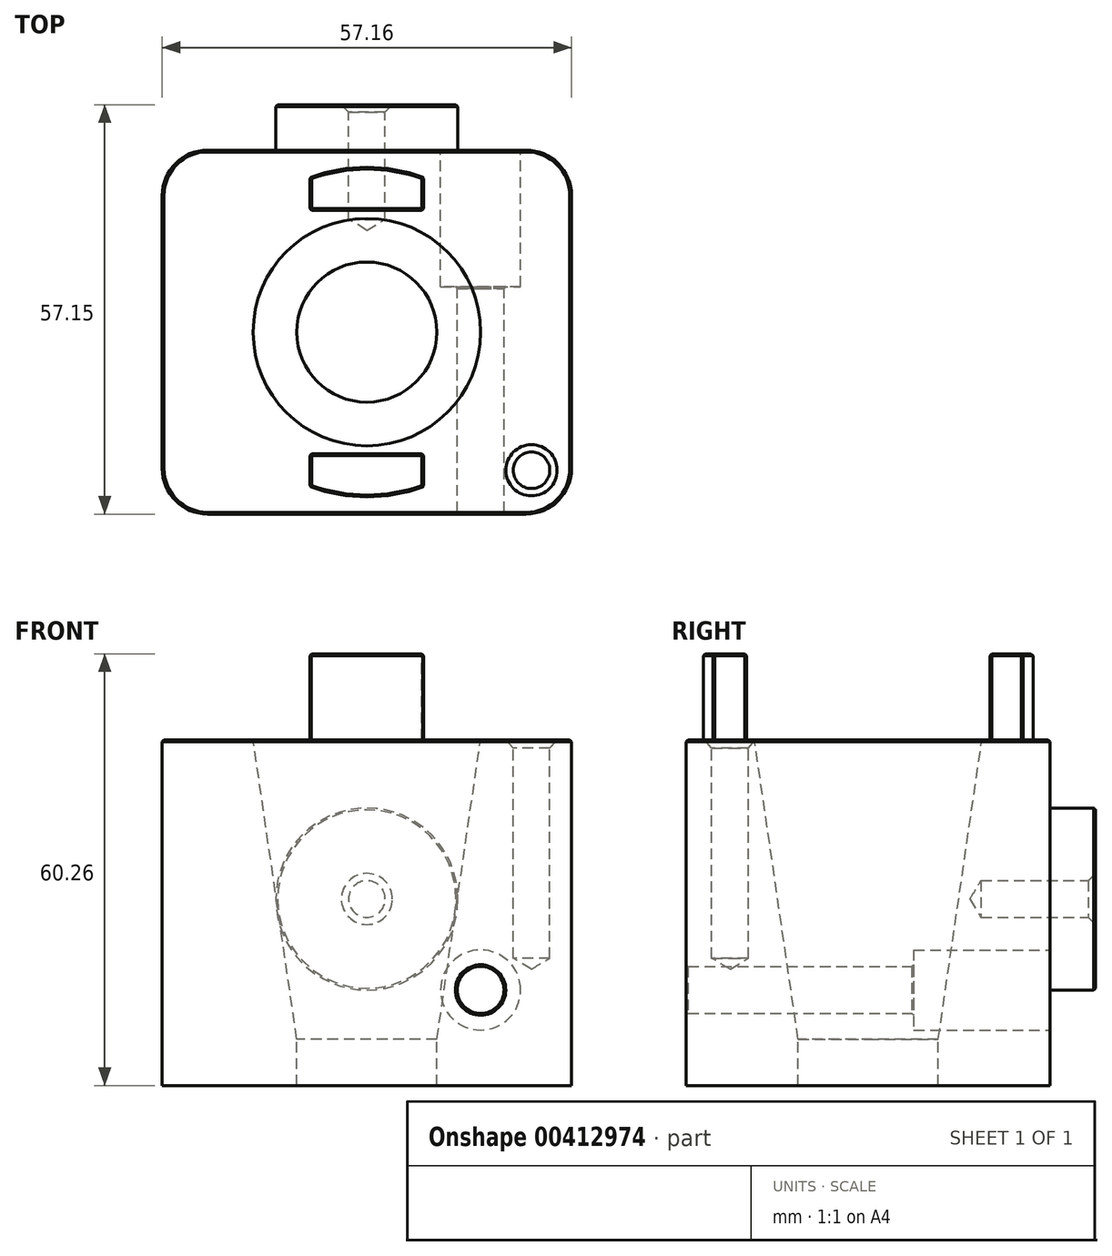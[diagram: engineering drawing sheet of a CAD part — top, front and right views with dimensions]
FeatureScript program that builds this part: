
annotation { "Feature Type Name" : "Feature", "Feature Type Description" : "" }
export const myFeature = defineFeature(function(context is Context, id is Id, definition is map)
    precondition{}
    {
        {
            var Q0;
            Q0=qCreatedBy(makeId("Top.planeOp"),FACE);
            var sketch = newSketch(context, id + "F0", { "sketchPlane" : qUnion([Q0])});
            skLineSegment(sketch, "E0.bottom", {"start": v(28.58, -25.4) * mm, "end": v(-28.58, -25.4) * mm});
            skLineSegment(sketch, "E0.top", {"start": v(28.58, 25.4) * mm, "end": v(-28.58, 25.4) * mm});
            skLineSegment(sketch, "E0.left", {"start": v(28.57, -25.4) * mm, "end": v(28.58, 25.4) * mm});
            skLineSegment(sketch, "E0.right", {"start": v(-28.58, -25.4) * mm, "end": v(-28.58, 25.4) * mm});
            skPoint(sketch, "E0.middle", {"position": v(0, 0) * mm});
            skSolve(sketch);
        }
        {
            var Q0;
            Q0 = qSketchRegion(id + "F0", true);
            extrude(context, id + "F1", {"entities" : qUnion([Q0]), "oppositeDirection" : true, "depth" : 48.26 * mm});
        }
        {
            var Q0;
            Q0=qCreatedBy(makeId("Front.planeOp"),FACE);
            var sketch = newSketch(context, id + "F2", { "sketchPlane" : qUnion([Q0])});
            skLineSegment(sketch, "E1", {"start": v(0, 0) * mm, "end": v(15.88, 0) * mm});
            skLineSegment(sketch, "E2", {"start": v(15.88, 0) * mm, "end": v(9.78, -41.8) * mm});
            skLineSegment(sketch, "E3", {"start": v(9.78, -48.4) * mm, "end": v(0, -48.4) * mm});
            skLineSegment(sketch, "E4", {"start": v(0, -48.4) * mm, "end": v(0, 0) * mm});
            skLineSegment(sketch, "E5", {"start": v(9.78, -48.4) * mm, "end": v(9.78, -41.8) * mm});
            skSolve(sketch);
        }
        {
            var Q0;
            Q0 = qSketchRegion(id + "F2", true);
            var Q1;
            Q1=sQuery(id+"F2.wireOp",EDGE,"E4");
            revolve(context, id + "F3", {"operationType" : NewBodyOperationType.REMOVE, "entities" : qUnion([Q0]), "axis" : qUnion([Q1]), "revolveType" : RevolveType.FULL, "oppositeDirection" : true});
        }
        {
            var Q0;
            Q0=makeQuery(id+"F1.opExtrude","CAP_FACE",FACE,{"disambiguationData":[OSD([sQuery(id+"F0.wireOp",EDGE,"E0.bottom"),sQuery(id+"F0.wireOp",EDGE,"E0.top"),sQuery(id+"F0.wireOp",EDGE,"E0.left"),sQuery(id+"F0.wireOp",EDGE,"E0.right")])],"isStart":true});
            var sketch = newSketch(context, id + "F4", { "sketchPlane" : qUnion([Q0])});
            skLineSegment(sketch, "E6", {"start": v(-7.94, 21.59) * mm, "end": v(-7.94, 17) * mm});
            skLineSegment(sketch, "E7", {"start": v(7.94, 21.59) * mm, "end": v(7.94, 17) * mm});
            skLineSegment(sketch, "E8", {"start": v(-7.94, 17) * mm, "end": v(7.94, 17) * mm});
            skLineSegment(sketch, "E9", {"start": v(-7.94, -17) * mm, "end": v(7.94, -17) * mm});
            skArc(sketch, "E10", {"start": v(7.94, 21.59) * mm, "mid": v(0, 23) * mm, "end": v(-7.94, 21.59) * mm});
            skArc(sketch, "E11.trimOffspring", {"start": v(-7.94, -21.59) * mm, "mid": v(0, -23) * mm, "end": v(7.94, -21.59) * mm});
            skLineSegment(sketch, "E12.trimOffspring", {"start": v(-7.94, -17) * mm, "end": v(-7.94, -21.59) * mm});
            skLineSegment(sketch, "E13.trimOffspring", {"start": v(7.94, -17) * mm, "end": v(7.94, -21.59) * mm});
            skSolve(sketch);
        }
        {
            var Q0;
            Q0 = qSketchRegion(id + "F4", true);
            extrude(context, id + "F5", {"entities" : qUnion([Q0]), "operationType" : NewBodyOperationType.ADD, "depth" : 12 * mm});
        }
        {
            var Q0;
            Q0=makeQuery(id+"F1.opExtrude","SWEPT_FACE",FACE,{"disambiguationData":[OSD([sQuery(id+"F0.wireOp",EDGE,"E0.top")])]});
            var sketch = newSketch(context, id + "F6", { "sketchPlane" : qUnion([Q0])});
            skCircle(sketch, "E14", {"center": v(-15.87, -34.93) * mm, "radius": 3.26 * mm});
            skSolve(sketch);
        }
        {
            var Q0;
            Q0 = qSketchRegion(id + "F6", true);
            extrude(context, id + "F7", {"entities" : qUnion([Q0]), "operationType" : NewBodyOperationType.REMOVE, "endBound" : BoundingType.THROUGH_ALL, "oppositeDirection" : true, "depth" : 25.4 * mm});
        }
        {
            var Q0;
            Q0=makeQuery(id+"F1.opExtrude","SWEPT_EDGE",EDGE,{"disambiguationData":[OSD([sQuery(id+"F0.wireOp",EDGE,"E0.bottom"),sQuery(id+"F0.wireOp",EDGE,"E0.right")])]});
            var Q1;
            Q1=makeQuery(id+"F1.opExtrude","SWEPT_EDGE",EDGE,{"disambiguationData":[OSD([sQuery(id+"F0.wireOp",EDGE,"E0.bottom"),sQuery(id+"F0.wireOp",EDGE,"E0.left")])]});
            var Q2;
            Q2=makeQuery(id+"F1.opExtrude","SWEPT_EDGE",EDGE,{"disambiguationData":[OSD([sQuery(id+"F0.wireOp",EDGE,"E0.top"),sQuery(id+"F0.wireOp",EDGE,"E0.left")])]});
            var Q3;
            Q3=makeQuery(id+"F1.opExtrude","SWEPT_EDGE",EDGE,{"disambiguationData":[OSD([sQuery(id+"F0.wireOp",EDGE,"E0.top"),sQuery(id+"F0.wireOp",EDGE,"E0.right")])]});
            fillet(context, id + "F8", {"entities" : qUnion([Q0, Q1, Q2, Q3]), "radius" : 6.35 * mm, "tangentPropagation" : true, "allowEdgeOverflow" : false});
        }
        {
            var Q0;
            Q0=makeQuery(id+"F1.opExtrude","CAP_FACE",FACE,{"disambiguationData":[OSD([sQuery(id+"F0.wireOp",EDGE,"E0.bottom"),sQuery(id+"F0.wireOp",EDGE,"E0.top"),sQuery(id+"F0.wireOp",EDGE,"E0.left"),sQuery(id+"F0.wireOp",EDGE,"E0.right")])],"isStart":true});
            var sketch = newSketch(context, id + "F9", { "sketchPlane" : qUnion([Q0])});
            skPoint(sketch, "E15", {"position": v(22.98, -19.28) * mm});
            skLineSegment(sketch, "E16", {"start": v(22.98, -19.28) * mm, "end": v(0, 0) * mm, "construction": true});
            skSolve(sketch);
        }
        {
            var Q0;
            Q0=sQuery(id+"F9.wireOp",VERTEX,"E15");
            var Q1;
            Q1=makeQuery(id+"F1.opExtrude","SWEPT_BODY",BODY,{"disambiguationData":[OSD([sQuery(id+"F0.wireOp",EDGE,"E0.bottom"),sQuery(id+"F0.wireOp",EDGE,"E0.top"),sQuery(id+"F0.wireOp",EDGE,"E0.left"),sQuery(id+"F0.wireOp",EDGE,"E0.right")])]});
            hole(context, id + "F10", {"style" : HoleStyle.C_SINK, "endStyle" : HoleEndStyle.BLIND, "holeDiameter" : 5.1 * mm, "cSinkDiameter" : 7.14 * mm, "cSinkAngle" : 82 * degree, "holeDepth" : 30.48 * mm, "isTappedThrough" : true, "tappedDepth" : 12.7 * mm, "tapClearance" : 3, "startFromSketch" : true, "locations" : qUnion([Q0]), "scope" : qUnion([Q1])});
        }
        {
            var Q0;
            Q0=makeQuery(id+"F1.opExtrude","SWEPT_FACE",FACE,{"disambiguationData":[OSD([sQuery(id+"F0.wireOp",EDGE,"E0.top")])]});
            var sketch = newSketch(context, id + "F11", { "sketchPlane" : qUnion([Q0])});
            skCircle(sketch, "E17", {"center": v(0, -22.23) * mm, "radius": 12.7 * mm});
            skSolve(sketch);
        }
        {
            var Q0;
            Q0 = qSketchRegion(id + "F11", true);
            extrude(context, id + "F12", {"entities" : qUnion([Q0]), "operationType" : NewBodyOperationType.ADD, "depth" : 6.35 * mm});
        }
        {
            var Q0;
            Q0=makeQuery(id+"F1.opExtrude","SWEPT_FACE",FACE,{"disambiguationData":[OSD([sQuery(id+"F0.wireOp",EDGE,"E0.top")])]});
            var sketch = newSketch(context, id + "F13", { "sketchPlane" : qUnion([Q0])});
            skCircle(sketch, "E18", {"center": v(-15.87, -34.93) * mm, "radius": 5.59 * mm});
            skSolve(sketch);
        }
        {
            var Q0;
            Q0 = qSketchRegion(id + "F13", true);
            extrude(context, id + "F14", {"entities" : qUnion([Q0]), "operationType" : NewBodyOperationType.REMOVE, "oppositeDirection" : true, "depth" : 19.05 * mm});
        }
        {
            var Q0;
            Q0=makeQuery(id+"F12.opExtrude","CAP_FACE",FACE,{"disambiguationData":[OSD([sQuery(id+"F11.wireOp",EDGE,"E17")])],"isStart":false});
            var sketch = newSketch(context, id + "F15", { "sketchPlane" : qUnion([Q0])});
            skPoint(sketch, "E19", {"position": v(0, -22.23) * mm});
            skSolve(sketch);
        }
        {
            var Q0;
            Q0=sQuery(id+"F15.wireOp",VERTEX,"E19");
            var Q1;
            Q1=makeQuery(id+"F1.opExtrude","SWEPT_BODY",BODY,{"disambiguationData":[OSD([sQuery(id+"F0.wireOp",EDGE,"E0.bottom"),sQuery(id+"F0.wireOp",EDGE,"E0.top"),sQuery(id+"F0.wireOp",EDGE,"E0.left"),sQuery(id+"F0.wireOp",EDGE,"E0.right")])]});
            hole(context, id + "F16", {"style" : HoleStyle.C_SINK, "endStyle" : HoleEndStyle.BLIND, "holeDiameter" : 5.1 * mm, "cSinkDiameter" : 7.14 * mm, "cSinkAngle" : 90 * degree, "holeDepth" : 16 * mm, "isTappedThrough" : true, "tappedDepth" : 12.7 * mm, "tapClearance" : 3, "startFromSketch" : true, "locations" : qUnion([Q0]), "scope" : qUnion([Q1])});
        }
        {
            var Q0;
            Q0=makeQuery(id+"F5.opExtrude","CAP_FACE",FACE,{"disambiguationData":[OSD([sQuery(id+"F4.wireOp",EDGE,"E9"),sQuery(id+"F4.wireOp",EDGE,"E11.trimOffspring"),sQuery(id+"F4.wireOp",EDGE,"E12.trimOffspring"),sQuery(id+"F4.wireOp",EDGE,"E13.trimOffspring")])],"isStart":false});
            var Q1;
            Q1=makeQuery(id+"F5.opExtrude","CAP_FACE",FACE,{"disambiguationData":[OSD([sQuery(id+"F4.wireOp",EDGE,"E6"),sQuery(id+"F4.wireOp",EDGE,"E7"),sQuery(id+"F4.wireOp",EDGE,"E8"),sQuery(id+"F4.wireOp",EDGE,"E10")])],"isStart":false});
            var Q2;
            Q2=makeQuery(id+"F5.opExtrude","SWEPT_EDGE",EDGE,{"disambiguationData":[OSD([sQuery(id+"F4.wireOp",EDGE,"E7"),sQuery(id+"F4.wireOp",EDGE,"E8")])]});
            var Q3;
            Q3=makeQuery(id+"F5.opExtrude","SWEPT_EDGE",EDGE,{"disambiguationData":[OSD([sQuery(id+"F4.wireOp",EDGE,"E9"),sQuery(id+"F4.wireOp",EDGE,"E13.trimOffspring")])]});
            var Q4;
            Q4=makeQuery(id+"F5.opExtrude","SWEPT_EDGE",EDGE,{"disambiguationData":[OSD([sQuery(id+"F4.wireOp",EDGE,"E6"),sQuery(id+"F4.wireOp",EDGE,"E8")])]});
            var Q5;
            Q5=makeQuery(id+"F5.opExtrude","SWEPT_EDGE",EDGE,{"disambiguationData":[OSD([sQuery(id+"F4.wireOp",EDGE,"E9"),sQuery(id+"F4.wireOp",EDGE,"E12.trimOffspring")])]});
            var Q6;
            Q6=makeQuery(id+"F5.opExtrude","SWEPT_EDGE",EDGE,{"disambiguationData":[OSD([sQuery(id+"F4.wireOp",EDGE,"E11.trimOffspring"),sQuery(id+"F4.wireOp",EDGE,"E12.trimOffspring")])]});
            var Q7;
            Q7=makeQuery(id+"F5.opExtrude","SWEPT_EDGE",EDGE,{"disambiguationData":[OSD([sQuery(id+"F4.wireOp",EDGE,"E6"),sQuery(id+"F4.wireOp",EDGE,"E10")])]});
            var Q8;
            Q8=makeQuery(id+"F5.opExtrude","SWEPT_EDGE",EDGE,{"disambiguationData":[OSD([sQuery(id+"F4.wireOp",EDGE,"E7"),sQuery(id+"F4.wireOp",EDGE,"E10")])]});
            var Q9;
            Q9=makeQuery(id+"F5.opExtrude","SWEPT_EDGE",EDGE,{"disambiguationData":[OSD([sQuery(id+"F4.wireOp",EDGE,"E11.trimOffspring"),sQuery(id+"F4.wireOp",EDGE,"E13.trimOffspring")])]});
            var Q10;
            Q10=makeQuery(id+"F1.opExtrude","CAP_EDGE",EDGE,{"disambiguationData":[OSD([sQuery(id+"F0.wireOp",EDGE,"E0.left")])],"isStart":true});
            var Q11;
            {var subQ0=sQuery(id+"F0.wireOp",EDGE,"E0.left");var subQ1=sQuery(id+"F0.wireOp",EDGE,"E0.top");Q11=makeQuery(id+"F8.opFillet","BLEND_EDGE",EDGE,{"blendedFrom":[makeQuery(id+"F1.opExtrude","SWEPT_EDGE",EDGE,{"disambiguationData":[OSD([subQ1,subQ0])]}),makeQuery(id+"F1.opExtrude","CAP_FACE",FACE,{"disambiguationData":[OSD([sQuery(id+"F0.wireOp",EDGE,"E0.bottom"),subQ1,subQ0,sQuery(id+"F0.wireOp",EDGE,"E0.right")])],"isStart":true})],"blendedInto":[makeQuery(id+"F1.opExtrude","CAP_FACE",FACE,{"disambiguationData":[OSD([sQuery(id+"F0.wireOp",EDGE,"E0.bottom"),subQ1,subQ0,sQuery(id+"F0.wireOp",EDGE,"E0.right")])],"isStart":true})]});}
            var Q12;
            Q12=makeQuery(id+"F12.opExtrude","CAP_EDGE",EDGE,{"disambiguationData":[OSD([sQuery(id+"F11.wireOp",EDGE,"E17")])],"isStart":false});
            var Q13;
            Q13=makeQuery(id+"F14.boolean.opBoolean","COPY",EDGE,{"derivedFrom":makeQuery(id+"F14.opExtrude","CAP_EDGE",EDGE,{"disambiguationData":[OSD([sQuery(id+"F13.wireOp",EDGE,"E18")])],"isStart":true})});
            var Q14;
            Q14=makeQuery(id+"F14.boolean.opBoolean","INTERSECT",EDGE,{"derivedFrom":[makeQuery(id+"F7.boolean.opBoolean","COPY",FACE,{"derivedFrom":makeQuery(id+"F7.opExtrude","SWEPT_FACE",FACE,{"disambiguationData":[OSD([sQuery(id+"F6.wireOp",EDGE,"E14")])]})}),makeQuery(id+"F14.opExtrude","CAP_FACE",FACE,{"disambiguationData":[OSD([sQuery(id+"F13.wireOp",EDGE,"E18")])],"isStart":false})]});
            var Q15;
            Q15=makeQuery(id+"F7.boolean.opBoolean","INTERSECT",EDGE,{"derivedFrom":[makeQuery(id+"F1.opExtrude","SWEPT_FACE",FACE,{"disambiguationData":[OSD([sQuery(id+"F0.wireOp",EDGE,"E0.bottom")])]}),makeQuery(id+"F7.opExtrude","SWEPT_FACE",FACE,{"disambiguationData":[OSD([sQuery(id+"F6.wireOp",EDGE,"E14")])]})]});
            chamfer(context, id + "F17", {"entities" : qUnion([Q0, Q1, Q2, Q3, Q4, Q5, Q6, Q7, Q8, Q9, Q10, Q11, Q12, Q13, Q14, Q15]), "width" : 0.25 * mm, "tangentPropagation" : true});
        }
        {
            var Q0;
            Q0=makeQuery(id+"F1.opExtrude","SWEPT_FACE",FACE,{"disambiguationData":[OSD([sQuery(id+"F0.wireOp",EDGE,"E0.top")])]});
            var sketch = newSketch(context, id + "F18", { "sketchPlane" : qUnion([Q0])});
            skCircle(sketch, "E20.0", {"center": v(0, -22.23) * mm, "radius": 12.7 * mm});
            skLineSegment(sketch, "E21.bottom", {"start": v(-38.1, -0.25) * mm, "end": v(38.1, -0.25) * mm});
            skLineSegment(sketch, "E21.top", {"start": v(-38.1, -76.45) * mm, "end": v(38.1, -76.45) * mm});
            skLineSegment(sketch, "E21.left", {"start": v(-38.1, -0.25) * mm, "end": v(-38.1, -76.45) * mm});
            skLineSegment(sketch, "E21.right", {"start": v(38.1, -0.25) * mm, "end": v(38.1, -76.45) * mm});
            skCircle(sketch, "E22", {"center": v(-15.87, -34.93) * mm, "radius": 3.18 * mm});
            skSolve(sketch);
        }
        {
            var Q0;
            Q0 = qSketchRegion(id + "F18", true);
            extrude(context, id + "F19", {"entities" : qUnion([Q0]), "depth" : 12.7 * mm});
        }
        {
            var Q0;
            Q0=makeQuery(id+"F19.opExtrude","SWEPT_FACE",FACE,{"disambiguationData":[OSD([sQuery(id+"F18.wireOp",EDGE,"E22")])]});
            var Q1;
            Q1=makeQuery(id+"F19.opExtrude","SWEPT_FACE",FACE,{"disambiguationData":[OSD([sQuery(id+"F18.wireOp",EDGE,"E20.0")])]});
            circularPattern(context, id + "F20", {"patternType" : PatternType.FACE, "faces" : qUnion([Q0]), "axis" : qUnion([Q1]), "angle" : 360 * degree, "instanceCount" : 4, "equalSpace" : true});
        }
        {
            var Q0;
            Q0=makeQuery(id+"F19.opExtrude","SWEPT_EDGE",EDGE,{"disambiguationData":[OSD([sQuery(id+"F18.wireOp",EDGE,"E21.bottom"),sQuery(id+"F18.wireOp",EDGE,"E21.left")])]});
            var Q1;
            Q1=makeQuery(id+"F19.opExtrude","SWEPT_EDGE",EDGE,{"disambiguationData":[OSD([sQuery(id+"F18.wireOp",EDGE,"E21.bottom"),sQuery(id+"F18.wireOp",EDGE,"E21.right")])]});
            fillet(context, id + "F21", {"entities" : qUnion([Q0, Q1]), "radius" : 25.4 * mm, "tangentPropagation" : true, "allowEdgeOverflow" : false});
        }
        {
            var Q0;
            Q0=makeQuery(id+"F19.opExtrude","SWEPT_FACE",FACE,{"disambiguationData":[OSD([sQuery(id+"F18.wireOp",EDGE,"E21.top")])]});
            var sketch = newSketch(context, id + "F22", { "sketchPlane" : qUnion([Q0])});
            skLineSegment(sketch, "E23.bottom", {"start": v(38.1, -25.4) * mm, "end": v(-38.1, -25.4) * mm});
            skLineSegment(sketch, "E23.top", {"start": v(38.1, -127) * mm, "end": v(-38.1, -127) * mm});
            skLineSegment(sketch, "E23.left", {"start": v(38.1, -25.4) * mm, "end": v(38.1, -127) * mm});
            skLineSegment(sketch, "E23.right", {"start": v(-38.1, -25.4) * mm, "end": v(-38.1, -127) * mm});
            skSolve(sketch);
        }
        {
            var Q0;
            Q0 = qSketchRegion(id + "F22", true);
            extrude(context, id + "F23", {"entities" : qUnion([Q0]), "depth" : 12.7 * mm});
        }
        {
            var Q0;
            Q0=makeQuery(id+"F23.opExtrude","SWEPT_BODY",BODY,{"disambiguationData":[OSD([sQuery(id+"F22.wireOp",EDGE,"E23.bottom"),sQuery(id+"F22.wireOp",EDGE,"E23.top"),sQuery(id+"F22.wireOp",EDGE,"E23.left"),sQuery(id+"F22.wireOp",EDGE,"E23.right")])]});
            deleteBodies(context, id + "F24", {"entities" : qUnion([Q0])});
        }
        {
            var Q0;
            Q0=makeQuery(id+"F19.opExtrude","SWEPT_BODY",BODY,{"disambiguationData":[OSD([sQuery(id+"F18.wireOp",EDGE,"E20.0"),sQuery(id+"F18.wireOp",EDGE,"E21.bottom"),sQuery(id+"F18.wireOp",EDGE,"E21.top"),sQuery(id+"F18.wireOp",EDGE,"E21.left"),sQuery(id+"F18.wireOp",EDGE,"E21.right"),sQuery(id+"F18.wireOp",EDGE,"E22")])]});
            deleteBodies(context, id + "F25", {"entities" : qUnion([Q0])});
        }
    });
